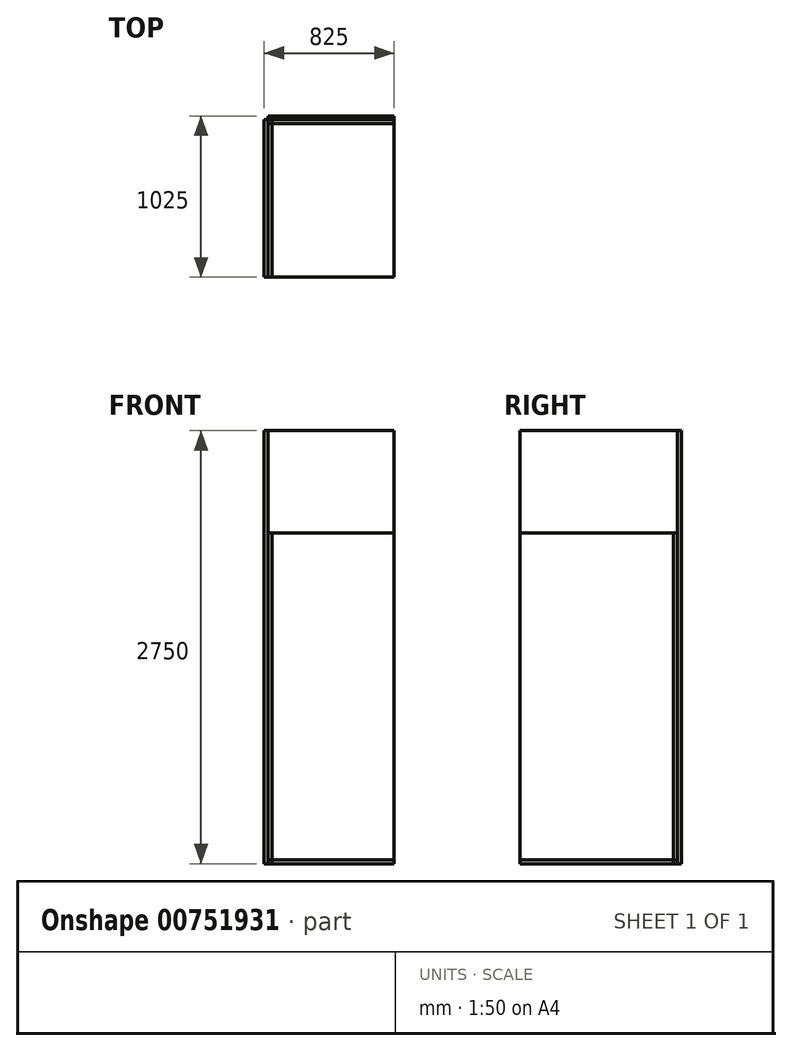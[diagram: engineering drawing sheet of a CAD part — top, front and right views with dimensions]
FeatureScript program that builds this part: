
annotation { "Feature Type Name" : "Feature", "Feature Type Description" : "" }
export const myFeature = defineFeature(function(context is Context, id is Id, definition is map)
    precondition{}
    {
        {
            var Q0;
            Q0=qCreatedBy(makeId("Front.planeOp"),FACE);
            var sketch = newSketch(context, id + "F0", { "sketchPlane" : qUnion([Q0])});
            skLineSegment(sketch, "E0.bottom", {"start": v(0, 0) * mm, "end": v(800, 0) * mm});
            skLineSegment(sketch, "E0.top", {"start": v(0, 2750) * mm, "end": v(800, 2750) * mm});
            skLineSegment(sketch, "E0.left", {"start": v(0, 0) * mm, "end": v(0, 2750) * mm});
            skLineSegment(sketch, "E0.right", {"start": v(800, 0) * mm, "end": v(800, 2750) * mm});
            skSolve(sketch);
        }
        {
            var Q0;
            Q0 = qSketchRegion(id + "F0", true);
            extrude(context, id + "F1", {"entities" : qUnion([Q0]), "oppositeDirection" : true, "depth" : 25 * mm, "offsetDistance" : 25 * mm});
        }
        {
            var Q0;
            Q0=qCreatedBy(makeId("Right.planeOp"),FACE);
            var sketch = newSketch(context, id + "F2", { "sketchPlane" : qUnion([Q0])});
            skLineSegment(sketch, "E1.bottom", {"start": v(0, 0) * mm, "end": v(-1000, 0) * mm});
            skLineSegment(sketch, "E1.top", {"start": v(0, 2750) * mm, "end": v(-1000, 2750) * mm});
            skLineSegment(sketch, "E1.left", {"start": v(0, 0) * mm, "end": v(0, 2750) * mm});
            skLineSegment(sketch, "E1.right", {"start": v(-1000, 0) * mm, "end": v(-1000, 2750) * mm});
            skSolve(sketch);
        }
        {
            var Q0;
            Q0 = qSketchRegion(id + "F2", true);
            extrude(context, id + "F3", {"entities" : qUnion([Q0]), "operationType" : NewBodyOperationType.ADD, "oppositeDirection" : true, "depth" : 25 * mm, "offsetDistance" : 25 * mm});
        }
        {
            var Q0;
            Q0=qCreatedBy(makeId("Top.planeOp"),FACE);
            var sketch = newSketch(context, id + "F4", { "sketchPlane" : qUnion([Q0])});
            skLineSegment(sketch, "E2.bottom", {"start": v(0, 0) * mm, "end": v(800, 0) * mm});
            skLineSegment(sketch, "E2.top", {"start": v(0, -1000) * mm, "end": v(800, -1000) * mm});
            skLineSegment(sketch, "E2.left", {"start": v(0, 0) * mm, "end": v(0, -1000) * mm});
            skLineSegment(sketch, "E2.right", {"start": v(800, 0) * mm, "end": v(800, -1000) * mm});
            skSolve(sketch);
        }
        {
            var Q0;
            Q0 = qSketchRegion(id + "F4", true);
            extrude(context, id + "F5", {"entities" : qUnion([Q0]), "depth" : 25 * mm, "offsetDistance" : 25 * mm});
        }
        {
            var Q0;
            Q0=makeQuery(id+"F1.opExtrude","CAP_FACE",FACE,{"disambiguationData":[OSD([sQuery(id+"F0.wireOp",EDGE,"E0.bottom"),sQuery(id+"F0.wireOp",EDGE,"E0.top"),sQuery(id+"F0.wireOp",EDGE,"E0.left"),sQuery(id+"F0.wireOp",EDGE,"E0.right")])],"isStart":true});
            var sketch = newSketch(context, id + "F6", { "sketchPlane" : qUnion([Q0])});
            skLineSegment(sketch, "E3.bottom", {"start": v(0, 0) * mm, "end": v(800, 0) * mm});
            skLineSegment(sketch, "E3.top", {"start": v(0, 2100) * mm, "end": v(800, 2100) * mm});
            skLineSegment(sketch, "E3.left", {"start": v(0, 0) * mm, "end": v(0, 2100) * mm});
            skLineSegment(sketch, "E3.right", {"start": v(800, 0) * mm, "end": v(800, 2100) * mm});
            skSolve(sketch);
        }
        {
            var Q0;
            Q0 = qSketchRegion(id + "F6", true);
            extrude(context, id + "F7", {"entities" : qUnion([Q0]), "depth" : 25 * mm, "offsetDistance" : 25 * mm});
        }
        {
            var Q0;
            Q0=makeQuery(id+"F3.opExtrude","CAP_FACE",FACE,{"disambiguationData":[OSD([sQuery(id+"F2.wireOp",EDGE,"E1.bottom"),sQuery(id+"F2.wireOp",EDGE,"E1.top"),sQuery(id+"F2.wireOp",EDGE,"E1.left"),sQuery(id+"F2.wireOp",EDGE,"E1.right")])],"isStart":true});
            var sketch = newSketch(context, id + "F8", { "sketchPlane" : qUnion([Q0])});
            skLineSegment(sketch, "E4.bottom", {"start": v(0, 0) * mm, "end": v(-1000, 0) * mm});
            skLineSegment(sketch, "E4.top", {"start": v(0, 2100) * mm, "end": v(-1000, 2100) * mm});
            skLineSegment(sketch, "E4.left", {"start": v(0, 0) * mm, "end": v(0, 2100) * mm});
            skLineSegment(sketch, "E4.right", {"start": v(-1000, 0) * mm, "end": v(-1000, 2100) * mm});
            skSolve(sketch);
        }
        {
            var Q0;
            Q0=makeQuery(id+"F8.imprint","IMPRINT",FACE,{"disambiguationData":[TD([[makeQuery(id+"F8.imprint","IMPRINT",EDGE,{"derivedFrom":sQuery(id+"F8.wireOp",EDGE,"E4.bottom")}),-1.0]])]});
            extrude(context, id + "F9", {"entities" : qUnion([Q0]), "depth" : 25 * mm, "offsetDistance" : 25 * mm});
        }
    });
